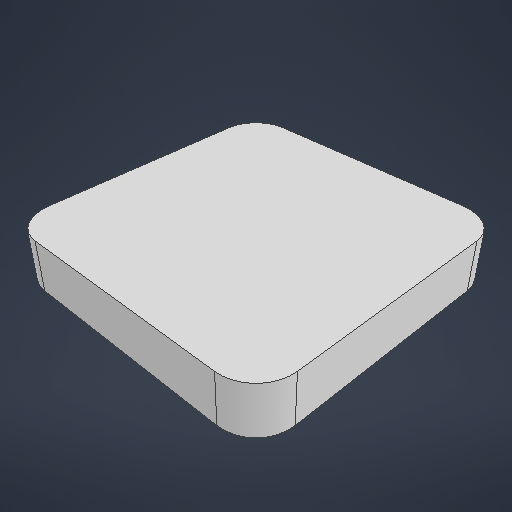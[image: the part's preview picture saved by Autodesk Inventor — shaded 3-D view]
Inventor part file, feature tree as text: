
AUTODESK INVENTOR PART (.ipt)
format: ipt  version: 2025.2 (Build 292293000, 293)  size: 205,312 bytes
history: native  units: mm
features: extrude x3, sketch x1
ambient origin geometry x8: Origin, YZ Plane, XZ Plane, XY Plane, X Axis, Y Axis, Z Axis, Center Point
bodies: Body1 (feature_tree)
feature tree (4):
  sketch  "Sketch1"  dims[d0=17.1mm d1=17.1mm d4=1.0mm d5=1.0mm d6=5.7mm d7=3.0mm d8=1.0mm d10=2.5mm d11=1.0mm d12=0.0mm d13=2.0mm d14=0.0mm d15=3.0mm d16=0.0mm d9=0.5mm]
  extrude  "Extrusion2"  Depth=17.1mm
  extrude  "Extrusion3"  Depth=1.0mm
  extrude  "Extrusion4"  Depth=1.0mm
